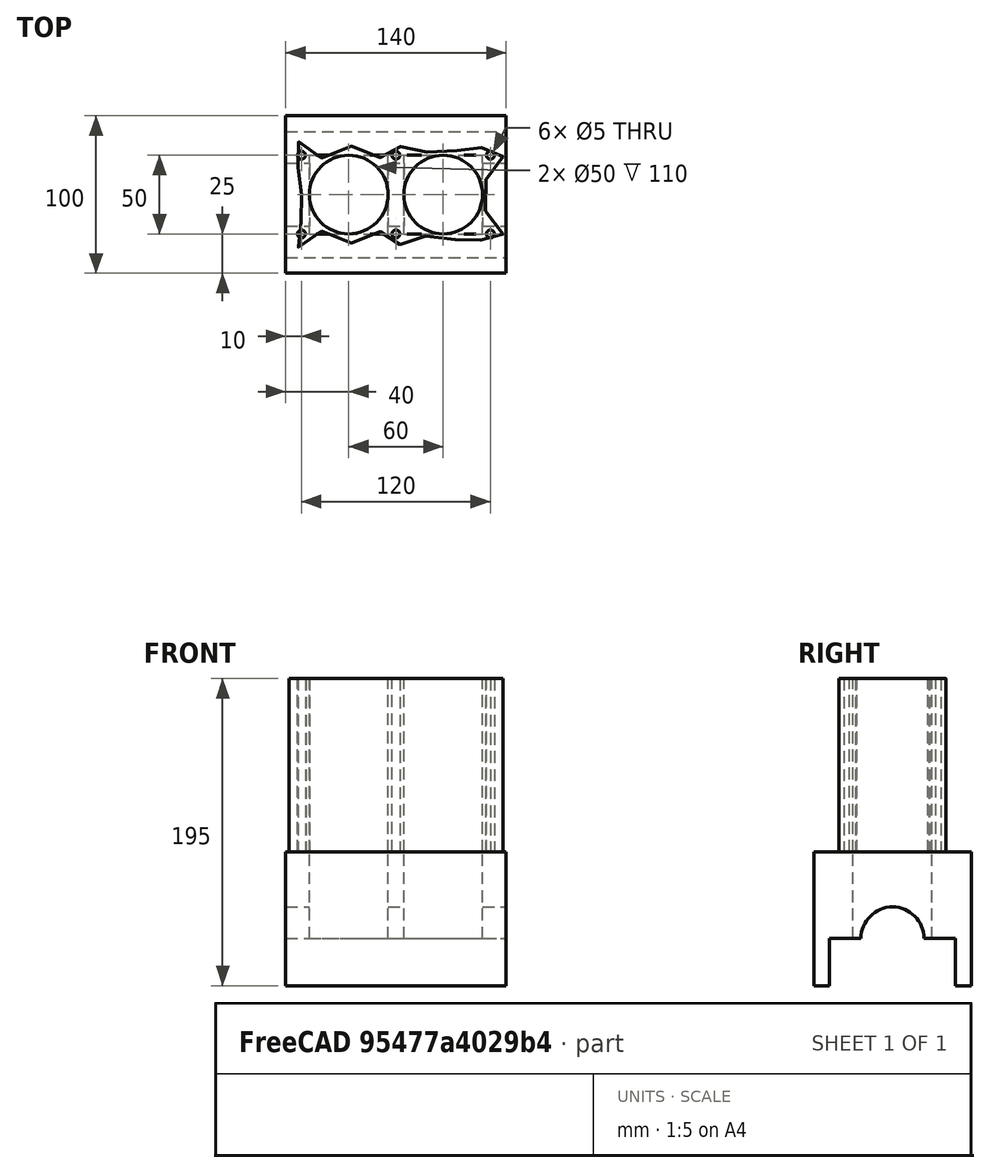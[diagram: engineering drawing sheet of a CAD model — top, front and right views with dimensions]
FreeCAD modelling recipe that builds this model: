
FCSTD DOCUMENT
Label: EngineBlock
License: CC-BY 3.0
LicenseURL: http://creativecommons.org/licenses/by/3.0/
objects: Part::Part2DObjectPython×8, Part::Extrusion×7, Part::Box×5, Part::Cut×5, Part::Cylinder×3, Part::MultiFuse×3, Part::Mirroring×3, App::DocumentObjectGroup×1, Part::MultiCommon×1
note: 35 computed .brp shape members not serialized (recipe doc carries the construction recipe); baked Part::Feature solids carry a one-line shape summary decoded from their .brp

FEATURE [Part::Box] Box  label="Billet"
  Height = 110
  Length = 140
  Placement = pos=(0,-40,0) rot=(0,0,1;0rad)
  Width = 80
FEATURE [Part::Cylinder] Cylinder  label="Cylinder 1"
  Angle = 360
  Height = 110
  Placement = pos=(40,0,0) rot=(0,0,1;0rad)
  Radius = 25
FEATURE [Part::Cylinder] Cylinder001  label="Cylinder 2"
  Angle = 360
  Height = 110
  Placement = pos=(100,0,0) rot=(0,0,1;0rad)
  Radius = 25
FEATURE [Part::MultiFuse] Fusion  label="Cylinders"
  Shapes = -> [Cylinder,Cylinder001]
FEATURE [Part::Cut] Cut  label="Bored Block"
  Base = -> Box
  Tool = -> Fusion
FEATURE [Part::Box] Box001  label="Crankcase Billet"
  Height = 85
  Length = 140
  Placement = pos=(0,-50,-85) rot=(0,0,1;0rad)
  Width = 100
FEATURE [Part::Box] Box002  label="Bearing carve"
  Height = 30
  Length = 140
  Placement = pos=(0,-40,-85) rot=(0,0,1;0rad)
  Width = 80
FEATURE [Part::Cut] Cut001  label="Carved crankcase"
  Base = -> Box001
  Tool = -> Box002
FEATURE [Part::Cylinder] Cylinder002  label="Cranshaft carve"
  Angle = 360
  Height = 140
  Placement = pos=(0,0,-55) rot=(0,1,0;1.5708rad)
  Radius = 20
FEATURE [Part::Cut] Cut002  label="Crankcase with journals"
  Base = -> Cut001
  Tool = -> Cylinder002
FEATURE [Part::Box] Box003  label="Box carve 1"
  Height = 55
  Length = 50
  Placement = pos=(15,-25,-55) rot=(0,0,1;0rad)
  Width = 50
FEATURE [Part::Box] Box004  label="Box carve 2"
  Height = 55
  Length = 50
  Placement = pos=(75,-25,-55) rot=(0,0,1;0rad)
  Width = 50
FEATURE [Part::MultiFuse] Fusion001  label="Box carvers"
  Shapes = -> [Box003,Box004]
FEATURE [Part::Cut] Cut003  label="Crankcase"
  Base = -> Cut002
  Tool = -> Fusion001
FEATURE [Part::Part2DObjectPython] Circle003  label="Bolt 007"  # Draft 2D object (typed FeaturePython)
  FirstAngle = 0
  LastAngle = 0
  Placement = pos=(10,25,110) rot=(0,0,1;0rad)
  Radius = 2.5
FEATURE [Part::Mirroring] Part__Mirroring  label="Bolt 4"
  Base = (0,0,0)
  Normal = (0,1,0)
  Source = -> Circle003
FEATURE [Part::Extrusion] Extrude  label="Head bolt bore 1"
  Base = -> Circle003
  Dir = (0,0,-110)
  Solid = false
FEATURE [Part::Extrusion] Extrude003  label="Head bolt bore 4"
  Base = -> Part__Mirroring
  Dir = (0,0,-110)
  Solid = false
FEATURE [Part::Part2DObjectPython] Circle004  label="Bolt 008"  # Draft 2D object (typed FeaturePython)
  FirstAngle = 0
  LastAngle = 0
  Placement = pos=(70,25,110) rot=(0,0,1;0rad)
  Radius = 2.5
FEATURE [Part::Mirroring] Part__Mirroring001  label="Bolt 5"
  Base = (0,0,0)
  Normal = (0,1,0)
  Source = -> Circle004
FEATURE [Part::Extrusion] Extrude001  label="Head bolt bore 2"
  Base = -> Circle004
  Dir = (0,0,-110)
  Solid = false
FEATURE [Part::Extrusion] Extrude004  label="Head bolt bore 5"
  Base = -> Part__Mirroring001
  Dir = (0,0,-110)
  Solid = false
FEATURE [Part::Part2DObjectPython] Circle005  label="Bolt 009"  # Draft 2D object (typed FeaturePython)
  FirstAngle = 0
  LastAngle = 0
  Placement = pos=(130,25,110) rot=(0,0,1;0rad)
  Radius = 2.5
FEATURE [Part::Mirroring] Part__Mirroring002  label="Bolt 6"
  Base = (0,0,0)
  Normal = (0,1,0)
  Source = -> Circle005
FEATURE [Part::Extrusion] Extrude002  label="Head bolt bore 3"
  Base = -> Circle005
  Dir = (0,0,-110)
  Solid = false
FEATURE [Part::Extrusion] Extrude005  label="Head bolt bore 6"
  Base = -> Part__Mirroring002
  Dir = (0,0,-110)
  Solid = false
FEATURE [Part::MultiFuse] Fusion002  label="Head bolt boreholes"
  Shapes = -> [Extrude,Extrude001,Extrude002,Extrude003,Extrude004,Extrude005]
FEATURE [Part::Cut] Cut004  label="Block with headbolts"
  Base = -> Cut
  Tool = -> Fusion002
FEATURE [Part::Part2DObjectPython] Polygon004  # Draft 2D object (typed FeaturePython)
  ChamferSize = 0
  DrawMode = 0
  FacesNumber = 14
  FilletRadius = 0
  Placement = pos=(40,0,110) rot=(0,0,1;0rad)
  Radius = 30
FEATURE [Part::Part2DObjectPython] Polygon005  # Draft 2D object (typed FeaturePython)
  ChamferSize = 0
  DrawMode = 0
  FacesNumber = 14
  FilletRadius = 0
  Placement = pos=(100,0,110) rot=(0,0,1;0rad)
  Radius = 30
FEATURE [Part::Part2DObjectPython] Polygon006  # Draft 2D object (typed FeaturePython)
  ChamferSize = 0
  DrawMode = 0
  FacesNumber = 22
  FilletRadius = 0
  Placement = pos=(40,0,110) rot=(0,0,1;0rad)
  Radius = 45
FEATURE [Part::Part2DObjectPython] Polygon007  # Draft 2D object (typed FeaturePython)
  ChamferSize = 0
  DrawMode = 0
  FacesNumber = 22
  FilletRadius = 0
  Placement = pos=(100,0,110) rot=(0,0,1;0rad)
  Radius = 45
FEATURE [App::DocumentObjectGroup] Construction
  Group = -> [Polygon004,Polygon005,Polygon006,Polygon007]
FEATURE [Part::Part2DObjectPython] BSpline001  # Draft 2D object (typed FeaturePython)
  Closed = true
FEATURE [Part::Extrusion] Extrude006  label="Extruded spline"
  Base = -> BSpline001
  Dir = (0,0,-110)
  Solid = false
FEATURE [Part::MultiCommon] Common  label="Engine block"
  Shapes = -> [Extrude006,Cut004]
